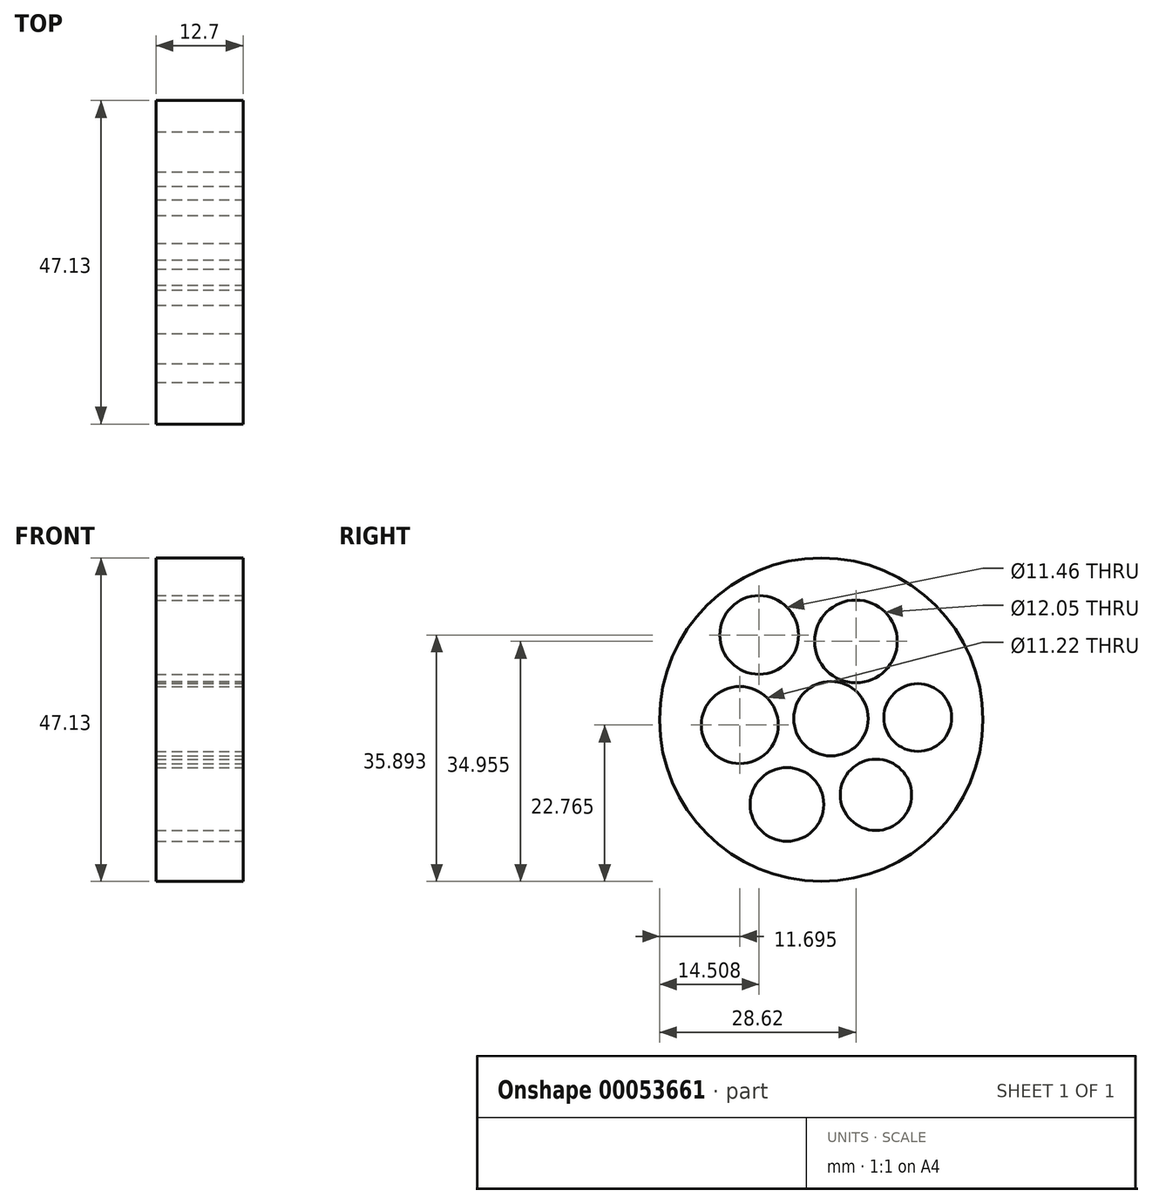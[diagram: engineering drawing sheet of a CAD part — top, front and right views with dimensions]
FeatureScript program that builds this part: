
annotation { "Feature Type Name" : "Feature", "Feature Type Description" : "" }
export const myFeature = defineFeature(function(context is Context, id is Id, definition is map)
    precondition{}
    {
        {
            var Q0;
            Q0=qCreatedBy(makeId("Right.planeOp"),FACE);
            var sketch = newSketch(context, id + "F0", { "sketchPlane" : qUnion([Q0])});
            skCircle(sketch, "E0", {"center": v(-5.05, 21.17) * mm, "radius": 23.56 * mm});
            skSolve(sketch);
        }
        {
            var Q0;
            Q0=makeQuery(id+"F0.imprint","IMPRINT",FACE,{"disambiguationData":[TD([[makeQuery(id+"F0.imprint","IMPRINT",EDGE,{"derivedFrom":sQuery(id+"F0.wireOp",EDGE,"E0")}),1.0]])]});
            extrude(context, id + "F1", {"entities" : qUnion([Q0]), "depth" : 12.7 * mm});
        }
        {
            var Q0;
            Q0=makeQuery(id+"F1.opExtrude","CAP_FACE",FACE,{"disambiguationData":[OSD([sQuery(id+"F0.wireOp",EDGE,"E0")])],"isStart":false});
            var sketch = newSketch(context, id + "F2", { "sketchPlane" : qUnion([Q0])});
            skCircle(sketch, "E1", {"center": v(-14.11, 33.5) * mm, "radius": 5.73 * mm});
            skCircle(sketch, "E2", {"center": v(-16.93, 20.38) * mm, "radius": 5.61 * mm});
            skCircle(sketch, "E3", {"center": v(-3.64, 21.31) * mm, "radius": 5.43 * mm});
            skCircle(sketch, "E4", {"center": v(9.02, 21.47) * mm, "radius": 4.93 * mm});
            skCircle(sketch, "E5", {"center": v(0, 32.57) * mm, "radius": 6.02 * mm});
            skCircle(sketch, "E6", {"center": v(-10.05, 8.81) * mm, "radius": 5.37 * mm});
            skCircle(sketch, "E7", {"center": v(2.92, 10.22) * mm, "radius": 5.2 * mm});
            skSolve(sketch);
        }
        {
            var Q0;
            Q0=makeQuery(id+"F2.imprint","IMPRINT",FACE,{"disambiguationData":[TD([[makeQuery(id+"F2.imprint","IMPRINT",EDGE,{"derivedFrom":sQuery(id+"F2.wireOp",EDGE,"E1")}),1.0]])]});
            var Q1;
            Q1=makeQuery(id+"F2.imprint","IMPRINT",FACE,{"disambiguationData":[TD([[makeQuery(id+"F2.imprint","IMPRINT",EDGE,{"derivedFrom":sQuery(id+"F2.wireOp",EDGE,"E5")}),1.0]])]});
            var Q2;
            Q2=makeQuery(id+"F2.imprint","IMPRINT",FACE,{"disambiguationData":[TD([[makeQuery(id+"F2.imprint","IMPRINT",EDGE,{"derivedFrom":sQuery(id+"F2.wireOp",EDGE,"E2")}),1.0]])]});
            var Q3;
            Q3=makeQuery(id+"F2.imprint","IMPRINT",FACE,{"disambiguationData":[TD([[makeQuery(id+"F2.imprint","IMPRINT",EDGE,{"derivedFrom":sQuery(id+"F2.wireOp",EDGE,"E3")}),1.0]])]});
            var Q4;
            Q4=makeQuery(id+"F2.imprint","IMPRINT",FACE,{"disambiguationData":[TD([[makeQuery(id+"F2.imprint","IMPRINT",EDGE,{"derivedFrom":sQuery(id+"F2.wireOp",EDGE,"E4")}),1.0]])]});
            var Q5;
            Q5=makeQuery(id+"F2.imprint","IMPRINT",FACE,{"disambiguationData":[TD([[makeQuery(id+"F2.imprint","IMPRINT",EDGE,{"derivedFrom":sQuery(id+"F2.wireOp",EDGE,"E7")}),1.0]])]});
            var Q6;
            Q6=makeQuery(id+"F2.imprint","IMPRINT",FACE,{"disambiguationData":[TD([[makeQuery(id+"F2.imprint","IMPRINT",EDGE,{"derivedFrom":sQuery(id+"F2.wireOp",EDGE,"E6")}),1.0]])]});
            extrude(context, id + "F3", {"entities" : qUnion([Q0, Q1, Q2, Q3, Q4, Q5, Q6]), "operationType" : NewBodyOperationType.REMOVE, "oppositeDirection" : true, "depth" : 25.4 * mm});
        }
    });
